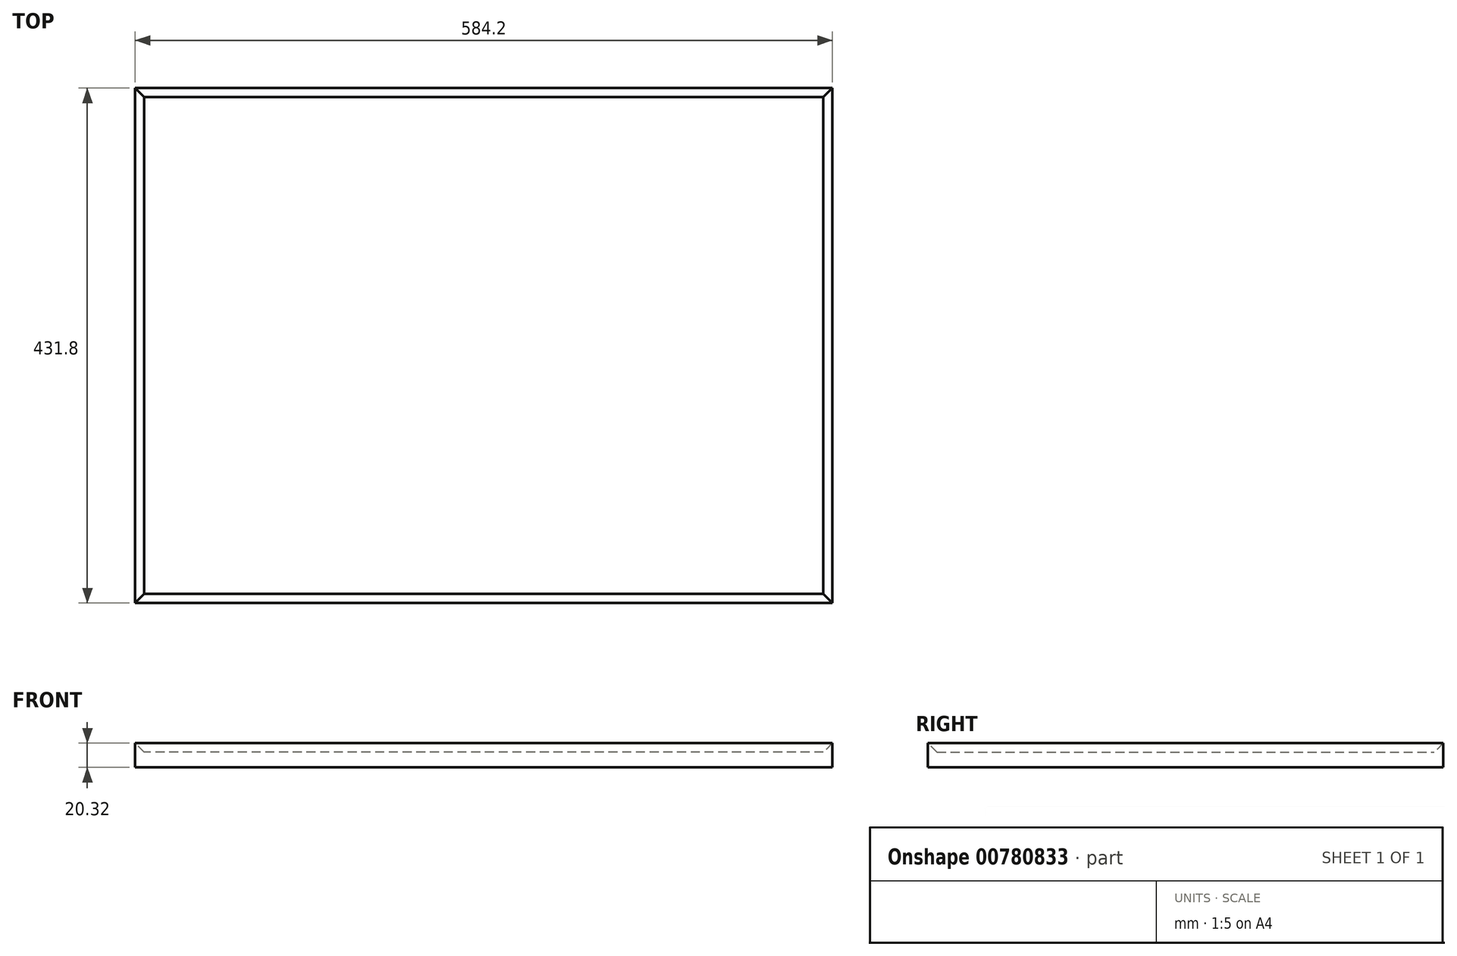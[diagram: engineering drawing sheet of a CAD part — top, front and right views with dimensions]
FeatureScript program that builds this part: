
annotation { "Feature Type Name" : "Feature", "Feature Type Description" : "" }
export const myFeature = defineFeature(function(context is Context, id is Id, definition is map)
    precondition{}
    {
        {
            var Q0;
            Q0=qCreatedBy(makeId("Top.planeOp"),FACE);
            var sketch = newSketch(context, id + "F0", { "sketchPlane" : qUnion([Q0])});
            skLineSegment(sketch, "E0.bottom", {"start": v(292.1, -215.9) * mm, "end": v(-292.1, -215.9) * mm});
            skLineSegment(sketch, "E0.top", {"start": v(292.1, 215.9) * mm, "end": v(-292.1, 215.9) * mm});
            skLineSegment(sketch, "E0.left", {"start": v(292.1, -215.9) * mm, "end": v(292.1, 215.9) * mm});
            skLineSegment(sketch, "E0.right", {"start": v(-292.1, -215.9) * mm, "end": v(-292.1, 215.9) * mm});
            skPoint(sketch, "E0.middle", {"position": v(0, 0) * mm});
            skSolve(sketch);
        }
        {
            var Q0;
            Q0 = qSketchRegion(id + "F0", true);
            extrude(context, id + "F1", {"entities" : qUnion([Q0]), "depth" : 12.7 * mm, "offsetDistance" : 25.4 * mm});
        }
        {
            var Q0;
            Q0=makeQuery(id+"F1.opExtrude","CAP_FACE",FACE,{"disambiguationData":[OSD([sQuery(id+"F0.wireOp",EDGE,"E0.bottom"),sQuery(id+"F0.wireOp",EDGE,"E0.top"),sQuery(id+"F0.wireOp",EDGE,"E0.left"),sQuery(id+"F0.wireOp",EDGE,"E0.right")])],"isStart":false});
            var sketch = newSketch(context, id + "F2", { "sketchPlane" : qUnion([Q0])});
            skLineSegment(sketch, "E1.bottom", {"start": v(-292.1, 215.9) * mm, "end": v(292.1, 215.9) * mm});
            skLineSegment(sketch, "E1.top", {"start": v(-292.1, -215.9) * mm, "end": v(292.1, -215.9) * mm});
            skLineSegment(sketch, "E1.left", {"start": v(-292.1, 215.9) * mm, "end": v(-292.1, -215.9) * mm});
            skLineSegment(sketch, "E1.right", {"start": v(292.1, 215.9) * mm, "end": v(292.1, -215.9) * mm});
            skLineSegment(sketch, "E2.bottom", {"start": v(-279.4, 203.2) * mm, "end": v(279.4, 203.2) * mm});
            skLineSegment(sketch, "E2.top", {"start": v(-279.4, -203.2) * mm, "end": v(279.4, -203.2) * mm});
            skLineSegment(sketch, "E2.left", {"start": v(-279.4, 203.2) * mm, "end": v(-279.4, -203.2) * mm});
            skLineSegment(sketch, "E2.right", {"start": v(279.4, 203.2) * mm, "end": v(279.4, -203.2) * mm});
            skSolve(sketch);
        }
        {
            var Q0;
            Q0=makeQuery(id+"F2.imprint","IMPRINT",FACE,{"disambiguationData":[TD([[makeQuery(id+"F2.imprint","IMPRINT",EDGE,{"derivedFrom":sQuery(id+"F2.wireOp",EDGE,"E1.bottom")}),1.0]])]});
            extrude(context, id + "F3", {"entities" : qUnion([Q0]), "operationType" : NewBodyOperationType.ADD, "depth" : 7.62 * mm, "offsetDistance" : 25.4 * mm});
        }
        {
            var Q0;
            Q0=makeQuery(id+"F3.opExtrude","CAP_EDGE",EDGE,{"disambiguationData":[OSD([sQuery(id+"F2.wireOp",EDGE,"E2.bottom")])],"isStart":false});
            var Q1;
            Q1=makeQuery(id+"F3.opExtrude","CAP_EDGE",EDGE,{"disambiguationData":[OSD([sQuery(id+"F2.wireOp",EDGE,"E2.right")])],"isStart":false});
            var Q2;
            Q2=makeQuery(id+"F3.opExtrude","CAP_EDGE",EDGE,{"disambiguationData":[OSD([sQuery(id+"F2.wireOp",EDGE,"E2.top")])],"isStart":false});
            var Q3;
            Q3=makeQuery(id+"F3.opExtrude","CAP_EDGE",EDGE,{"disambiguationData":[OSD([sQuery(id+"F2.wireOp",EDGE,"E2.left")])],"isStart":false});
            chamfer(context, id + "F4", {"entities" : qUnion([Q0, Q1, Q2, Q3]), "width" : 12.7 * mm, "tangentPropagation" : true});
        }
    });
